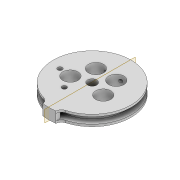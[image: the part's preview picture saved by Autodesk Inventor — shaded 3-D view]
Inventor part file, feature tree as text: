
AUTODESK INVENTOR PART (.ipt)
format: ipt  version: 2022 (Build 260153000, 153)  size: 347,648 bytes
history: native  units: mm
features: extrude x8, sketch x7, plane x3, fillet x2, mirror x2, pattern_circular x1, projected_geometry x1
ambient origin geometry x8: Origin, YZ Plane, XZ Plane, XY Plane, X Axis, Y Axis, Z Axis, Center Point
bodies: Solid1 (feature_tree)
feature tree (24):
  extrude  "Extrusion1"  Depth=30.0mm
  extrude  "Extrusion2"  Depth=3.0mm TaperAngle=0.0deg
  pattern_circular  "Circular Pattern1"  Count=5 Angle=360.0deg
  plane  "Work Plane1"
  plane  "Work Plane2"
  extrude  "Extrusion3"  [1 undecoded]
  extrude  "Extrusion4"  Depth=3.0mm
  fillet  "Fillet1"  Radius=1.7mm
  plane  "Work Plane3"
  extrude  "Extrusion5"  Depth=10.0mm TaperAngle=0.0deg
  mirror  "Mirror1"
  sketch  "Sketch6"  dims[d13=9.599311mm d14=-9.599311mm]
  extrude  "Extrusion6"  Depth=3.0mm
  extrude  "Extrusion7"  Depth=3.0mm
  extrude  "Extrusion8"  Depth=3.0mm
  fillet  "Fillet2"  Radius=10.0mm
  mirror  "Mirror2"
  sketch  "Sketch1"  dims[d0=4.2mm d2=30.0mm]
  sketch  "Sketch2"  dims[d3=4.0mm d4=3.0mm d5=0.0mm]
  sketch  "Sketch3"  dims[d6=7.0mm]
  sketch  "Sketch4"  dims[d7=8.0mm]
  sketch  "Sketch5"  dims[d8=10.0mm d9=0.0mm d10=50.0mm d11=360.0deg]
  projected_geometry  "Projected Loop1"
  sketch  "Sketch7"  dims[d15=1.5mm d16=1.5mm d17=1.7mm d18=10.0mm d19=0.0mm d20=1.5mm d21=1.5mm d22=1.7mm d23=10.0mm d24=0.0mm d25=1.0mm d26=36.0mm d27=1.0mm d28=0.0mm d29=2.1mm d30=13.0mm d31=1.9mm d32=2.1mm d33=8.4mm d35=5.0mm d36=0.0mm d37=100.0mm d38=0.0mm d39=4.5mm d40=3.0mm d41=3.0mm d42=2.0mm d43=5.0mm d44=0.0mm d45=3.0mm]
note: 1 required parameter value undecoded (feature->parameter linkage not recoverable at this tier; creation-order binding heuristic only, values carry confidence <= 0.55)
